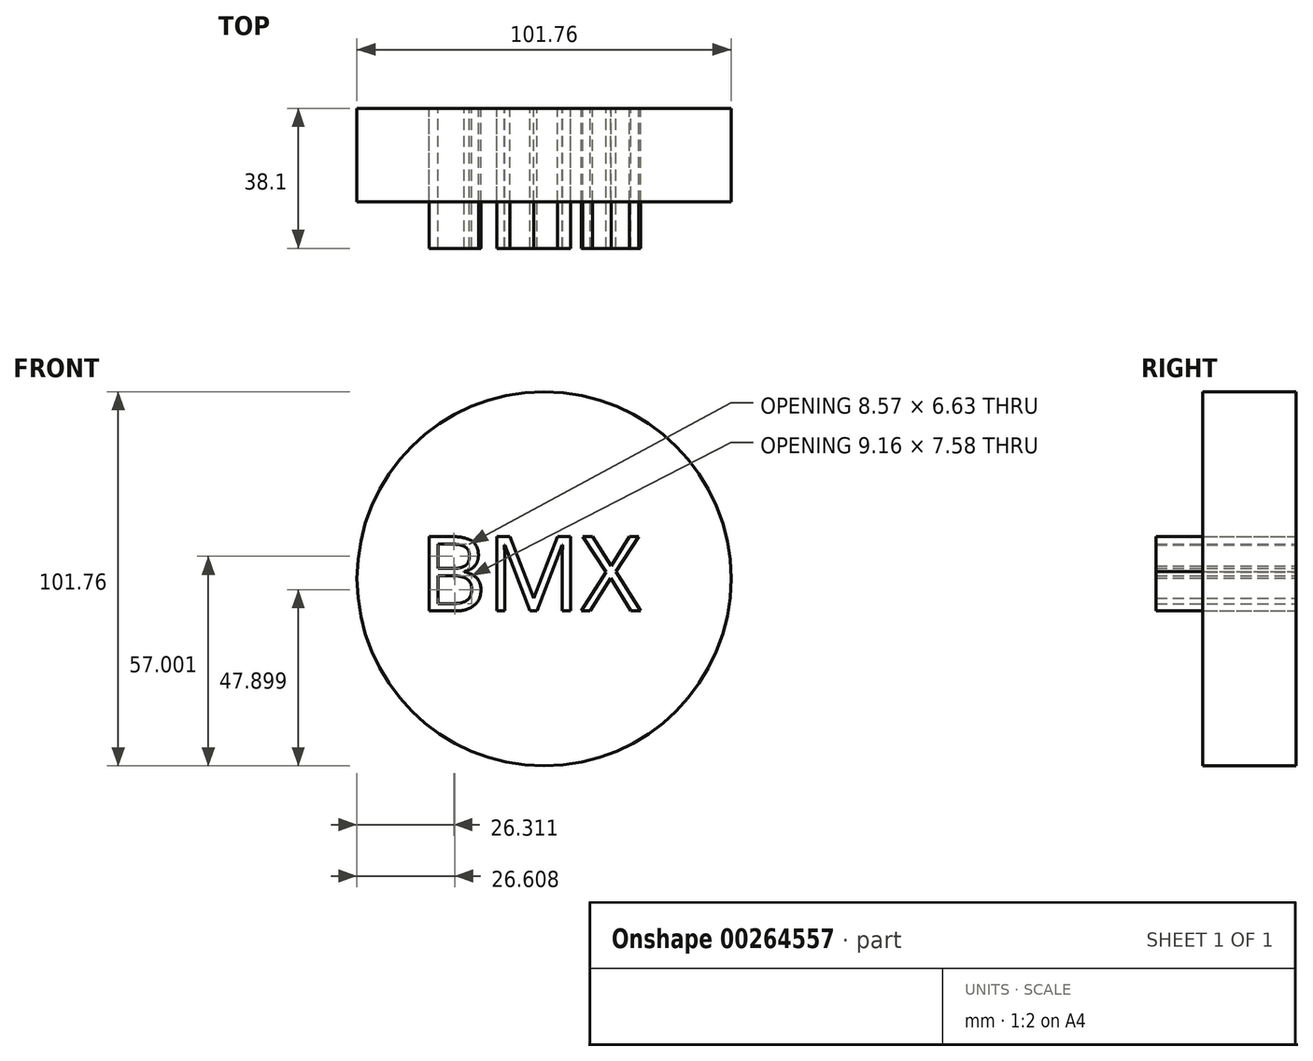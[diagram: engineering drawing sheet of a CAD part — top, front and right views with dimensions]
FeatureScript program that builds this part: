
annotation { "Feature Type Name" : "Feature", "Feature Type Description" : "" }
export const myFeature = defineFeature(function(context is Context, id is Id, definition is map)
    precondition{}
    {
        {
            var Q0;
            Q0=qCreatedBy(makeId("Front.planeOp"),FACE);
            var sketch = newSketch(context, id + "F0", { "sketchPlane" : qUnion([Q0])});
            skCircle(sketch, "E0", {"center": v(0, 0) * mm, "radius": 50.88 * mm});
            skSolve(sketch);
        }
        {
            var Q0;
            Q0=makeQuery(id+"F0.imprint","IMPRINT",FACE,{"disambiguationData":[TD([[makeQuery(id+"F0.imprint","IMPRINT",EDGE,{"derivedFrom":sQuery(id+"F0.wireOp",EDGE,"E0")}),1.0]])]});
            var sketch = newSketch(context, id + "F1", { "sketchPlane" : qUnion([Q0])});
            skText(sketch, "E1", { "text": "BMX", "fontName": "OpenSans-Regular.ttf"});
            const initialGuessF1  = {"E1": [-0.03399, -0.00878, 1, 0, 0.02043]};
            skSetInitialGuess(sketch, initialGuessF1);
            skSolve(sketch);
        }
        {
            var Q0;
            Q0 = qSketchRegion(id + "F1", true);
            extrude(context, id + "F2", {"entities" : qUnion([Q0]), "depth" : 38.1 * mm});
        }
        {
            var Q0;
            Q0=makeQuery(id+"F0.imprint","IMPRINT",FACE,{"disambiguationData":[TD([[makeQuery(id+"F0.imprint","IMPRINT",EDGE,{"derivedFrom":sQuery(id+"F0.wireOp",EDGE,"E0")}),1.0]])]});
            extrude(context, id + "F3", {"entities" : qUnion([Q0]), "depth" : 25.4 * mm});
        }
    });
